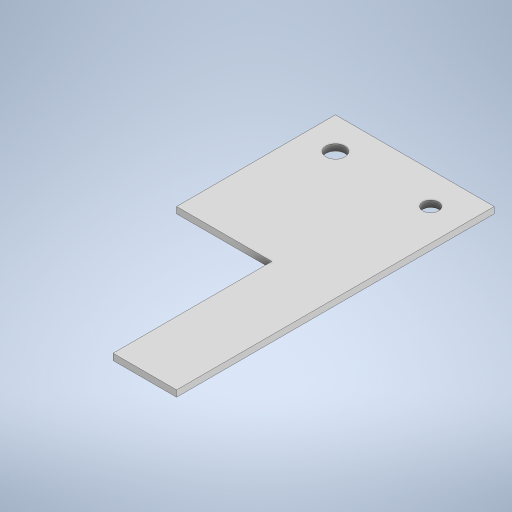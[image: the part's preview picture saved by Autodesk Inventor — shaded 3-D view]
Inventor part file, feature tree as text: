
AUTODESK INVENTOR PART (.ipt)
format: ipt  version: 2023 (Build 270158000, 158)  size: 233,984 bytes
history: native  units: mm
features: extrude x1, sketch x1
ambient origin geometry x8: Origin, YZ Plane, XZ Plane, XY Plane, X Axis, Y Axis, Z Axis, Center Point
bodies: Solid1 (feature_tree)
feature tree (2):
  extrude  "Extrusion1"  Depth=50.0mm
  sketch  "Sketch1"  dims[d0=50.0mm d1=50.0mm d2=20.0mm d3=50.0mm d4=10.0mm d5=10.0mm d6=10.0mm d7=10.0mm d8=6.0mm d9=5.0mm d10=2.0mm d11=0.0mm]
